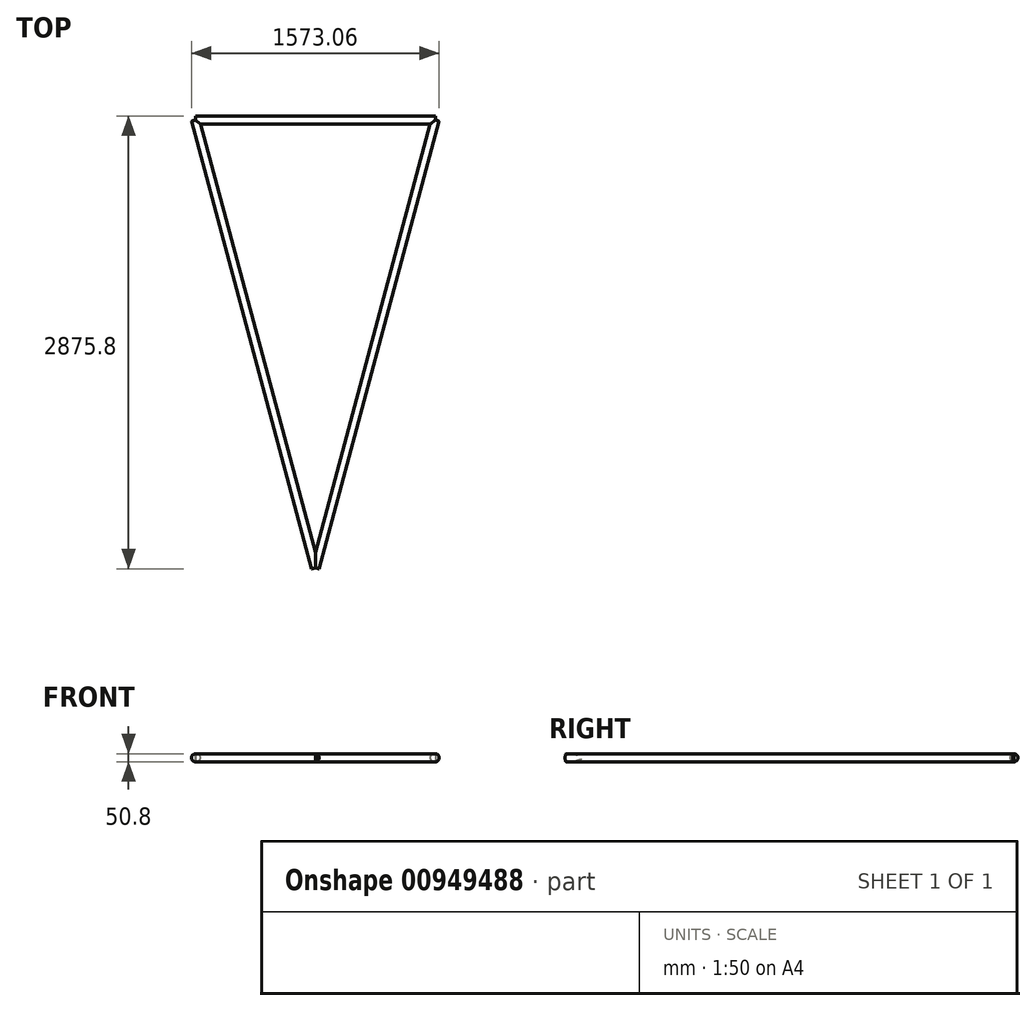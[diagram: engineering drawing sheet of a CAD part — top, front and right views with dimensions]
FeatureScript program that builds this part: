
annotation { "Feature Type Name" : "Feature", "Feature Type Description" : "" }
export const myFeature = defineFeature(function(context is Context, id is Id, definition is map)
    precondition{}
    {
        {
            var Q0;
            Q0=qCreatedBy(makeId("Top.planeOp"),FACE);
            var sketch = newSketch(context, id + "F0", { "sketchPlane" : qUnion([Q0])});
            skLineSegment(sketch, "E0", {"start": v(0, -952.9) * mm, "end": v(762, 1890.92) * mm});
            skLineSegment(sketch, "E1", {"start": v(0, -952.9) * mm, "end": v(-762, 1890.92) * mm});
            skLineSegment(sketch, "E2", {"start": v(-762, 1890.92) * mm, "end": v(762, 1890.92) * mm});
            skLineSegment(sketch, "E3", {"start": v(0, -952.9) * mm, "end": v(0, 1890.92) * mm});
            skLineSegment(sketch, "E4", {"start": v(-381, 469) * mm, "end": v(381, 469) * mm});
            skLineSegment(sketch, "E5", {"start": v(-571.5, 1179.96) * mm, "end": v(571.5, 1179.96) * mm});
            skSolve(sketch);
        }
        {
            var Q0;
            Q0=sQuery(id+"F0.wireOp",EDGE,"E0");
            extrude(context, id + "F1", {"bodyType" : ToolBodyType.SURFACE, "operationType" : NewBodyOperationType.REMOVE, "surfaceEntities" : qUnion([Q0]), "depth" : 25.4 * mm, "offsetDistance" : 25.4 * mm});
        }
        {
            var Q0;
            Q0=makeQuery(id+"F1.opExtrude","SWEPT_FACE",FACE,{"disambiguationData":[OSD([sQuery(id+"F0.wireOp",EDGE,"E0")])]});
            var Q1;
            Q1=makeQuery(id+"F1.opExtrude","CAP_EDGE",EDGE,{"disambiguationData":[OSD([sQuery(id+"F0.wireOp",EDGE,"E0")])],"isStart":true});
            revolve(context, id + "F2", {"surfaceOperationType" : NewSurfaceOperationType.NEW, "entities" : qUnion([Q0]), "axis" : qUnion([Q1]), "revolveType" : RevolveType.FULL});
        }
        {
            var Q0;
            Q0=sQuery(id+"F0.wireOp",EDGE,"E1");
            extrude(context, id + "F3", {"bodyType" : ToolBodyType.SURFACE, "surfaceEntities" : qUnion([Q0]), "depth" : 25.4 * mm, "offsetDistance" : 25.4 * mm});
        }
        {
            var Q0;
            Q0=sQuery(id+"F0.wireOp",EDGE,"E2");
            extrude(context, id + "F4", {"bodyType" : ToolBodyType.SURFACE, "surfaceEntities" : qUnion([Q0]), "depth" : 25.4 * mm, "offsetDistance" : 25.4 * mm});
        }
        {
            var Q0;
            Q0=makeQuery(id+"F4.opExtrude","SWEPT_FACE",FACE,{"disambiguationData":[OSD([sQuery(id+"F0.wireOp",EDGE,"E2")])]});
            var Q1;
            Q1=sQuery(id+"F0.wireOp",EDGE,"E2");
            revolve(context, id + "F5", {"operationType" : NewBodyOperationType.ADD, "surfaceOperationType" : NewSurfaceOperationType.NEW, "entities" : qUnion([Q0]), "axis" : qUnion([Q1]), "revolveType" : RevolveType.FULL});
        }
        {
            var Q0;
            Q0=makeQuery(id+"F3.opExtrude","SWEPT_FACE",FACE,{"disambiguationData":[OSD([sQuery(id+"F0.wireOp",EDGE,"E1")])]});
            var Q1;
            Q1=sQuery(id+"F0.wireOp",EDGE,"E1");
            revolve(context, id + "F6", {"operationType" : NewBodyOperationType.ADD, "surfaceOperationType" : NewSurfaceOperationType.NEW, "entities" : qUnion([Q0]), "axis" : qUnion([Q1]), "revolveType" : RevolveType.FULL});
        }
    });
